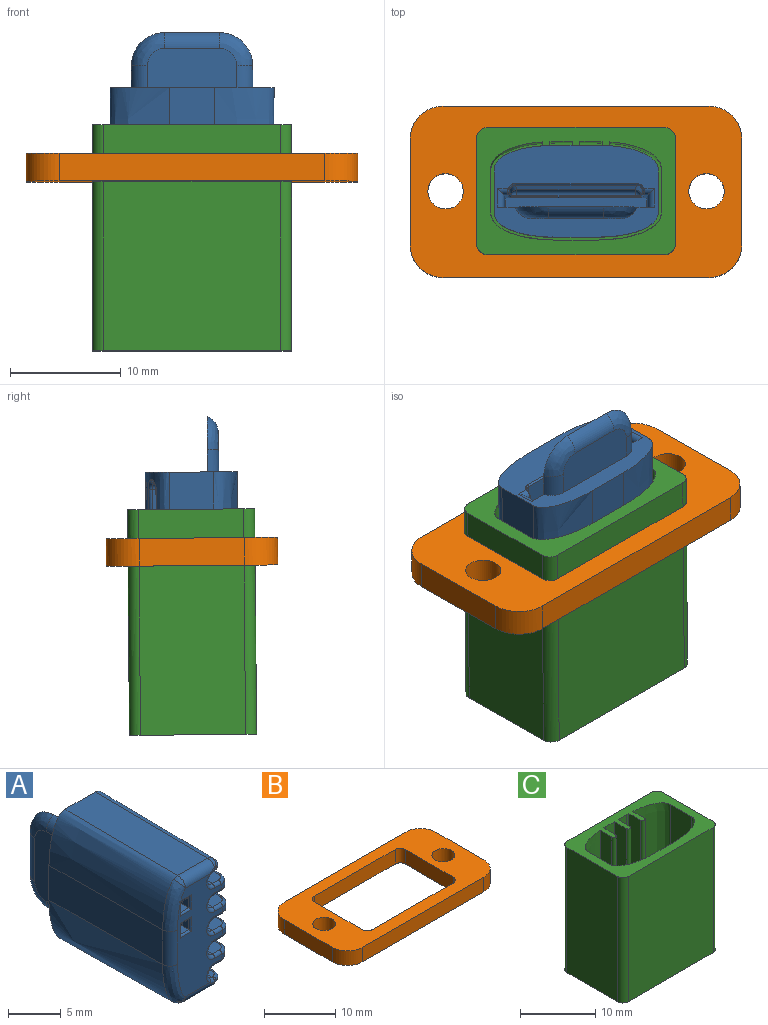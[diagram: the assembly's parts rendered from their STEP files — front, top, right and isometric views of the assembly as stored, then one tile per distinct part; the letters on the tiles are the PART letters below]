
ASSEMBLY  parts=3 mates=2
PART A: 179 faces, bbox 8.4x21.2x14.9 mm
  f0: bspline ~0.31x0.21mm, area 0.1mm2, adj f19,f94,f103,f104
  f1: bspline ~1.11x1mm, area 0.9mm2, adj f13,f20,f159,f178
  f2: cylinder r=1mm len=1mm, axis (0,0,1), area 0.9mm2, adj f18,f20,f138,f155
  f3: bspline ~0.91x0.75mm, area 0.3mm2, adj f17,f51,f134
  f4: plane 8.34x1.18mm, normal (0,-0.02,1), area 5.8mm2, adj f9,f21,f29,f37,f40,f53,f54
  f5: plane 8.34x1.18mm, normal (0,-0.02,-1), area 5.8mm2, adj f9,f21,f29,f37,f40,f53,f56
  f6: plane 8.34x1.18mm, normal (0,-0.02,1), area 5.8mm2, adj f8,f21,f28,f38,f39,f60,f62
  f7: plane 8.34x1.18mm, normal (0,-0.02,-1), area 5.8mm2, adj f8,f21,f28,f38,f39,f59,f60
  f8: plane 1x0.02mm, normal (0.01,-1,0), area 0mm2, adj f6,f7,f21,f39
  f9: plane 1x0.02mm, normal (0.01,-1,0), area 0mm2, adj f4,f5,f21,f40
  f10: plane 12.79x0.85mm, normal (0,1,0), area 10.9mm2, adj f21,f22,f23,f26,f28,f29
  f11: bspline ~16.06x5.41mm, area 92.3mm2, adj f14,f15,f19,f42,f44
  f12: bspline ~16.06x5.41mm, area 92.3mm2, adj f15,f16,f19,f48,f50
  f13: bspline ~16.06x5.41mm, area 34.3mm2, adj f1,f14,f18,f19,f43,f45,f156,f157
  f14: plane 15.07x4.02mm, normal (0,-0.01,-1), area 60.5mm2, adj f11,f13,f19,f41
  f15: plane 15.07x4.02mm, normal (-1,-0.01,0), area 60.5mm2, adj f11,f12,f19,f46
  f16: plane 15.07x4.02mm, normal (0,-0.01,1), area 60.5mm2, adj f12,f17,f19,f52
  f17: bspline ~16.06x5.41mm, area 34.3mm2, adj f3,f16,f18,f19,f49,f51,f124,f126
  f18: plane 15.1x4.04mm, normal (1,-0.01,0), area 23.2mm2, adj f2,f13,f17,f19,f47,f135,f136,f146
  f19: plane 14.85x8.32mm, normal (0,1,0), area 73.6mm2, adj f0,f11,f12,f13,f14,f15,f16,f17
  f20: plane 12.57x6.04mm, normal (0,-1,0), area 47.9mm2, adj f1,f2,f41,f44,f46,f47,f48,f49
  f21: plane 20.08x14.17mm, normal (1,0.01,0), area 228.8mm2, adj f4,f5,f6,f7,f8,f9,f10,f19
  f22: plane 14.51x1.11mm, normal (0,0.01,-1), area 14.2mm2, adj f10,f21,f23,f69
  f23: plane 14.54x13.07mm, normal (-1,0.01,0), area 14.7mm2, adj f10,f22,f26,f32,f33,f34,f35,f36
  f24: plane 13.79x0.28mm, normal (0,0.01,-1), area 1.4mm2, adj f31,f32,f98,f100
  f25: plane 13.79x0.28mm, normal (0,0.01,1), area 1.4mm2, adj f30,f36,f94,f106
  f26: plane 14.51x1.11mm, normal (0,0.01,1), area 14.2mm2, adj f10,f21,f23,f71
  f27: plane 10.7x0.05mm, normal (0,1,0), area 0.5mm2, adj f30,f31,f34,f96
  f28: plane 1.3x0.81mm, normal (-1,-0.01,0), area 1mm2, adj f6,f7,f10,f60
  f29: plane 1.3x0.81mm, normal (-1,-0.01,0), area 1mm2, adj f4,f5,f10,f53
  f30: cylinder r=0.55mm len=0.55mm, axis (1,0,0), area 0mm2, adj f25,f27,f35,f95
  f31: cylinder r=0.55mm len=0.55mm, axis (-1,0,0), area 0mm2, adj f24,f27,f33,f97
  f32: cylinder r=0.15mm len=13.49mm, axis (-0.01,-1,-0.01), area 3.2mm2, adj f23,f24,f33,f99
  f33: bspline ~0.7x0.7mm, area 0.2mm2, adj f23,f31,f32,f34
  f34: cylinder r=0.15mm len=10.7mm, axis (0,0,-1), area 2.5mm2, adj f23,f27,f33,f35
  f35: bspline ~0.7x0.7mm, area 0.2mm2, adj f23,f30,f34,f36
  f36: cylinder r=0.15mm len=13.49mm, axis (-0.01,-1,0.01), area 3.2mm2, adj f23,f25,f35,f107
  f37: plane 8.17x1.3mm, normal (0.99,-0.11,0), area 9.5mm2, adj f4,f5,f40,f54,f56,f57,f58
  f38: plane 8.17x1.3mm, normal (0.99,-0.11,0), area 9.5mm2, adj f6,f7,f39,f59,f61,f62
  f39: cylinder r=0.2mm len=1.01mm, axis (0,0,1), area 0.3mm2, adj f6,f7,f8,f38
  f40: cylinder r=0.2mm len=1.01mm, axis (0,0,-1), area 0.3mm2, adj f4,f5,f9,f37
  f41: cylinder r=1mm len=4.02mm, axis (1,0,0), area 6.1mm2, adj f14,f20,f42,f43,f171,f173
  f42: bspline ~1x1mm, area 0.6mm2, adj f11,f41,f44
  f43: bspline ~0.94x0.73mm, area 0.5mm2, adj f13,f41,f45,f169
  f44: bspline ~5.13x2.08mm, area 8mm2, adj f11,f20,f42,f46
  f45: bspline ~0.91x0.76mm, area 0.3mm2, adj f13,f43,f167
  f46: cylinder r=1mm len=4.02mm, axis (0,0,-1), area 6.3mm2, adj f15,f20,f44,f48
  f47: cylinder r=1mm len=1mm, axis (0,0,1), area 0.9mm2, adj f18,f20,f148,f166
  f48: bspline ~5.09x2.07mm, area 8mm2, adj f12,f20,f46,f50,f55,f58
  f49: bspline ~1.11x1mm, area 0.9mm2, adj f17,f20,f123,f145
  f50: bspline ~1x1mm, area 0.4mm2, adj f12,f48,f52
  f51: bspline ~0.94x0.73mm, area 0.5mm2, adj f3,f17,f52,f133
  f52: cylinder r=1mm len=4.02mm, axis (-1,0,0), area 6.1mm2, adj f16,f20,f50,f51,f129,f131
  f53: cylinder r=0.2mm len=1.7mm, axis (0,0,1), area 0.5mm2, adj f4,f5,f20,f29,f54,f56
  f54: cylinder r=0.2mm len=1.58mm, axis (1,0,0), area 0.4mm2, adj f4,f20,f37,f53,f57
  f55: bspline ~0.11x0.1mm, area 0mm2, adj f48,f56,f58
  f56: cylinder r=0.2mm len=1.5mm, axis (-1,0,0), area 0.4mm2, adj f5,f20,f37,f53,f55,f58
  f57: cylinder r=0.2mm len=1.4mm, axis (0,0,-1), area 0.4mm2, adj f20,f37,f54,f58
  f58: bspline ~0.3x0.22mm, area 0.1mm2, adj f37,f48,f55,f56,f57
  f59: cylinder r=0.2mm len=1.58mm, axis (-1,0,0), area 0.4mm2, adj f7,f20,f38,f60,f61
  f60: cylinder r=0.2mm len=1.7mm, axis (0,0,1), area 0.5mm2, adj f6,f7,f20,f28,f59,f62
  f61: cylinder r=0.2mm len=1.7mm, axis (0,0,-1), area 0.4mm2, adj f20,f38,f59,f62
  f62: cylinder r=0.2mm len=1.58mm, axis (1,0,0), area 0.4mm2, adj f6,f20,f38,f60,f61
  f63: plane 8.07x3.57mm, normal (-1,0.01,0), area 27.7mm2, adj f19,f64,f65,f66,f67,f68
  f64: cylinder r=1.56mm len=2.05mm, axis (0.01,1,0), area 3.9mm2, adj f19,f21,f63,f65
  f65: bspline ~3x2.97mm, area 6.9mm2, adj f21,f63,f64,f66
  f66: cylinder r=1.56mm len=4.98mm, axis (0,0,-1), area 9.2mm2, adj f21,f63,f65,f67
  f67: bspline ~3x2.97mm, area 6.9mm2, adj f21,f63,f66,f68
  f68: cylinder r=1.56mm len=2.04mm, axis (0.01,1,0), area 3.9mm2, adj f19,f21,f63,f67
  f69: cylinder r=0.55mm len=1.66mm, axis (1,0,0), area 1.2mm2, adj f19,f21,f22,f70
  f70: cylinder r=0.55mm len=0.94mm, axis (0,0,-1), area 0.5mm2, adj f19,f23,f69,f99,f100,f101
  f71: cylinder r=0.55mm len=1.66mm, axis (-1,0,0), area 1.2mm2, adj f19,f21,f26,f72
  f72: cylinder r=0.55mm len=0.94mm, axis (0,0,-1), area 0.5mm2, adj f19,f23,f71,f105,f106,f107
  f73: plane 13.87x10.94mm, normal (-1,0.02,0), area 150.1mm2, adj f94,f96,f98,f103
  f74: plane 1.89x0.11mm, normal (0,-1,0), area 0.2mm2, adj f117,f118,f119,f139
  f75: cone r=0.6mm half-angle=0.5deg, axis (0,-1,0), area 29.7mm2, adj f76,f77,f118,f142
  f76: plane 14.17x1.85mm, normal (0,-0.01,1), area 25.2mm2, adj f75,f119,f136,f138,f140
  f77: plane 14.17x1.74mm, normal (0,-0.01,-1), area 23.6mm2, adj f75,f117,f143,f144,f145
  f78: plane 1.43x0.11mm, normal (0,-1,0), area 0.1mm2, adj f120,f121,f122,f128
  f79: cone r=0.6mm half-angle=0.5deg, axis (0,-1,0), area 29.7mm2, adj f80,f81,f121,f127,f129
  f80: plane 14.18x0.97mm, normal (0,-0.01,-1), area 11.3mm2, adj f79,f120,f131,f132,f133,f134
  f81: plane 14.18x1.61mm, normal (0,-0.01,1), area 22mm2, adj f79,f122,f123,f124,f125
  f82: plane 1.89x0.11mm, normal (0,-1,0), area 0.2mm2, adj f111,f112,f113,f158
  f83: cone r=0.6mm half-angle=0.5deg, axis (0,-1,0), area 29.7mm2, adj f84,f85,f112,f163
  f84: plane 14.17x1.74mm, normal (0,-0.01,1), area 23.6mm2, adj f83,f113,f157,f159,f161
  f85: plane 14.17x1.85mm, normal (0,-0.01,-1), area 25.2mm2, adj f83,f111,f164,f165,f166
  f86: plane 1.91x0.11mm, normal (0,-1,0), area 0.2mm2, adj f114,f115,f116,f149
  f87: cone r=0.6mm half-angle=0.5deg, axis (0,-1,0), area 29.7mm2, adj f88,f89,f115,f152
  f88: plane 14.17x1.85mm, normal (0,-0.01,-1), area 25.2mm2, adj f87,f114,f153,f154,f155
  f89: plane 14.17x1.85mm, normal (0,-0.01,1), area 25.2mm2, adj f87,f116,f146,f148,f150
  f90: plane 1.43x0.11mm, normal (0,-1,0), area 0.1mm2, adj f108,f109,f110,f172
  f91: cone r=0.6mm half-angle=0.5deg, axis (0,-1,0), area 29.7mm2, adj f92,f93,f109,f173,f175
  f92: plane 14.18x1.61mm, normal (0,-0.01,-1), area 22mm2, adj f91,f108,f176,f177,f178
  f93: plane 14.18x0.97mm, normal (0,-0.01,1), area 11.3mm2, adj f91,f110,f167,f168,f169,f171
  f94: cylinder r=0.55mm len=13.88mm, axis (0.02,1,-0.01), area 12mm2, adj f0,f25,f73,f95,f104,f105
  f95: sphere r=0.55mm, area 0.3mm2, adj f30,f94,f96
  f96: cylinder r=0.55mm len=10.7mm, axis (0,0,1), area 9.2mm2, adj f27,f73,f95,f97
  f97: sphere r=0.55mm, area 0.3mm2, adj f31,f96,f98
  f98: cylinder r=0.55mm len=13.87mm, axis (-0.02,-1,-0.01), area 12mm2, adj f24,f73,f97,f101,f102
  f99: cylinder r=0.15mm len=0.15mm, axis (0.01,1,0.01), area 0mm2, adj f32,f70,f100
  f100: bspline ~0.42x0.32mm, area 0.1mm2, adj f24,f70,f99,f101
  f101: bspline ~0.32x0.22mm, area 0.1mm2, adj f70,f98,f100,f102
  f102: bspline ~0.66x0.52mm, area 0.2mm2, adj f19,f98,f101,f103
  f103: cylinder r=0.15mm len=10.94mm, axis (0,0,1), area 2.5mm2, adj f0,f19,f73,f102
  f104: bspline ~0.44x0.42mm, area 0.1mm2, adj f0,f19,f94,f105
  f105: bspline ~0.32x0.22mm, area 0.1mm2, adj f72,f94,f104,f106
  f106: bspline ~0.42x0.32mm, area 0.1mm2, adj f25,f72,f105,f107
  f107: bspline ~0.15x0.15mm, area 0mm2, adj f36,f72,f106
  f108: cylinder r=0.55mm len=1.61mm, axis (-1,0,0), area 1.3mm2, adj f90,f92,f109,f174
  f109: torus R=0.05mm, axis (0,1,0), area 1.1mm2, adj f90,f91,f108,f110
  f110: cylinder r=0.55mm len=1.34mm, axis (1,0,0), area 1mm2, adj f90,f93,f109,f170
  f111: cylinder r=0.55mm len=1.85mm, axis (-1,0,0), area 1.6mm2, adj f82,f85,f112,f160,f162
  f112: torus R=0.05mm, axis (0,1,0), area 1.1mm2, adj f82,f83,f111,f113
  f113: cylinder r=0.55mm len=1.83mm, axis (1,0,0), area 1.5mm2, adj f82,f84,f112,f156
  f114: cylinder r=0.55mm len=1.85mm, axis (-1,0,0), area 1.6mm2, adj f86,f88,f115,f151
  f115: torus R=0.05mm, axis (0,1,0), area 1.1mm2, adj f86,f87,f114,f116
  f116: cylinder r=0.55mm len=1.85mm, axis (1,0,0), area 1.6mm2, adj f86,f89,f115,f147
  f117: cylinder r=0.55mm len=1.83mm, axis (-1,0,0), area 1.5mm2, adj f74,f77,f118,f141
  f118: torus R=0.05mm, axis (0,1,0), area 1.1mm2, adj f74,f75,f117,f119
  f119: cylinder r=0.55mm len=1.85mm, axis (1,0,0), area 1.6mm2, adj f74,f76,f118,f135,f137
  f120: cylinder r=0.55mm len=1.34mm, axis (-1,0,0), area 1mm2, adj f78,f80,f121,f130
  f121: torus R=0.05mm, axis (0,1,0), area 1.1mm2, adj f78,f79,f120,f122
  f122: cylinder r=0.55mm len=1.61mm, axis (1,0,0), area 1.3mm2, adj f78,f81,f121,f126
  f123: bspline ~1.01x1mm, area 0.7mm2, adj f49,f81,f124,f125
  f124: cylinder r=0.35mm len=13.52mm, axis (0.01,1,0.01), area 6.5mm2, adj f17,f81,f123,f126
  f125: cylinder r=0.35mm len=0.84mm, axis (-1,0,0), area 0.5mm2, adj f20,f81,f123,f127
  f126: bspline ~0.94x0.9mm, area 0.6mm2, adj f17,f122,f124,f128
  f127: torus R=1.08mm, axis (0,1,0), area 1.2mm2, adj f20,f79,f125,f129
  f128: cylinder r=0.35mm len=0.37mm, axis (-0.32,0,0.95), area 0.1mm2, adj f17,f78,f126,f130
  f129: bspline ~0.65x0.62mm, area 0.4mm2, adj f52,f79,f127,f131
  f130: bspline ~1.09x0.9mm, area 0.7mm2, adj f17,f120,f128,f132
  f131: cylinder r=0.35mm len=0.47mm, axis (-1,0,0), area 0mm2, adj f52,f80,f129,f133
  f132: bspline ~13.53x0.85mm, area 10.2mm2, adj f17,f80,f130,f134
  f133: bspline ~0.51x0.47mm, area 0.1mm2, adj f51,f80,f131,f134
  f134: bspline ~0.93x0.88mm, area 0.9mm2, adj f3,f80,f132,f133
  f135: bspline ~0.62x0.5mm, area 0.3mm2, adj f18,f119,f136,f137
  f136: cylinder r=0.35mm len=13.52mm, axis (0.01,1,0.01), area 7.4mm2, adj f18,f76,f135,f138
  f137: bspline ~0.67x0.52mm, area 0.3mm2, adj f17,f119,f135,f139
  f138: bspline ~1x1mm, area 0.7mm2, adj f2,f76,f136,f140
  f139: cylinder r=0.35mm len=0.36mm, axis (-0.05,0,1), area 0.1mm2, adj f17,f74,f137,f141
  f140: cylinder r=0.35mm len=1.07mm, axis (-1,0,0), area 0.6mm2, adj f20,f76,f138,f142
  f141: bspline ~0.95x0.9mm, area 0.6mm2, adj f17,f117,f139,f143
  f142: torus R=1.08mm, axis (0,1,0), area 1.5mm2, adj f20,f75,f140,f144
  f143: cylinder r=0.35mm len=13.52mm, axis (-0.01,-1,0.01), area 8.1mm2, adj f17,f77,f141,f145
  f144: cylinder r=0.35mm len=0.94mm, axis (1,0,0), area 0.5mm2, adj f20,f77,f142,f145
  f145: bspline ~1.01x1mm, area 0.8mm2, adj f49,f77,f143,f144
  f146: cylinder r=0.35mm len=13.52mm, axis (0.01,1,0.01), area 7.4mm2, adj f18,f89,f147,f148
  f147: bspline ~0.9x0.9mm, area 0.6mm2, adj f18,f116,f146,f149
  f148: bspline ~1x1mm, area 0.7mm2, adj f47,f89,f146,f150
  f149: cylinder r=0.35mm len=0.35mm, axis (0,0,1), area 0.1mm2, adj f18,f86,f147,f151
  f150: cylinder r=0.35mm len=1.07mm, axis (-1,0,0), area 0.6mm2, adj f20,f89,f148,f152
  f151: bspline ~0.9x0.9mm, area 0.6mm2, adj f18,f114,f149,f153
  f152: torus R=1.08mm, axis (0,1,0), area 1.5mm2, adj f20,f87,f150,f154
  f153: cylinder r=0.35mm len=13.52mm, axis (-0.01,-1,0.01), area 7.4mm2, adj f18,f88,f151,f155
  f154: cylinder r=0.35mm len=1.07mm, axis (1,0,0), area 0.6mm2, adj f20,f88,f152,f155
  f155: bspline ~1x1mm, area 0.7mm2, adj f2,f88,f153,f154
  f156: bspline ~0.95x0.9mm, area 0.6mm2, adj f13,f113,f157,f158
  f157: cylinder r=0.35mm len=13.52mm, axis (0.01,1,0.01), area 8.1mm2, adj f13,f84,f156,f159
  f158: cylinder r=0.35mm len=0.36mm, axis (0.05,0,1), area 0.1mm2, adj f13,f82,f156,f160
  f159: bspline ~1.06x1mm, area 0.8mm2, adj f1,f84,f157,f161
  f160: bspline ~0.67x0.52mm, area 0.3mm2, adj f13,f111,f158,f162
  f161: cylinder r=0.35mm len=0.94mm, axis (-1,0,0), area 0.5mm2, adj f20,f84,f159,f163
  f162: bspline ~0.62x0.5mm, area 0.3mm2, adj f18,f111,f160,f164
  f163: torus R=1.08mm, axis (0,1,0), area 1.5mm2, adj f20,f83,f161,f165
  f164: cylinder r=0.35mm len=13.52mm, axis (-0.01,-1,0.01), area 7.4mm2, adj f18,f85,f162,f166
  f165: cylinder r=0.35mm len=1.07mm, axis (1,0,0), area 0.6mm2, adj f20,f85,f163,f166
  f166: bspline ~1x1mm, area 0.7mm2, adj f47,f85,f164,f165
  f167: bspline ~1.23x1.07mm, area 0.9mm2, adj f45,f93,f168,f169
  f168: bspline ~13.53x0.85mm, area 10.2mm2, adj f13,f93,f167,f170
  f169: bspline ~0.47x0.37mm, area 0.1mm2, adj f43,f93,f167,f171
  f170: bspline ~1.09x0.9mm, area 0.7mm2, adj f13,f110,f168,f172
  f171: cylinder r=0.35mm len=0.47mm, axis (1,0,0), area 0mm2, adj f41,f93,f169,f173
  f172: cylinder r=0.35mm len=0.37mm, axis (0.32,0,0.95), area 0.1mm2, adj f13,f90,f170,f174
  f173: bspline ~0.65x0.62mm, area 0.4mm2, adj f41,f91,f171,f175
  f174: bspline ~0.94x0.9mm, area 0.6mm2, adj f13,f108,f172,f176
  f175: torus R=1.08mm, axis (0,1,0), area 1.2mm2, adj f20,f91,f173,f177
  f176: cylinder r=0.35mm len=13.52mm, axis (-0.01,-1,0.01), area 6.5mm2, adj f13,f92,f174,f178
  f177: cylinder r=0.35mm len=0.84mm, axis (1,0,0), area 0.5mm2, adj f20,f92,f175,f178
  f178: bspline ~1.01x1mm, area 0.7mm2, adj f1,f92,f176,f177
PART B: 20 faces, bbox 30x15.5x2.5 mm
  f0: plane 24x2.5mm, normal (0,-1,0), area 60mm2, adj f1,f17,f18,f19
  f1: cylinder r=3mm len=3mm, axis (0,0,1), area 11.8mm2, adj f0,f2,f18,f19
  f2: plane 9.5x2.5mm, normal (1,0,0), area 23.8mm2, adj f1,f3,f18,f19
  f3: cylinder r=3mm len=3mm, axis (0,0,1), area 11.8mm2, adj f2,f4,f18,f19
  f4: plane 24x2.5mm, normal (0,1,0), area 60mm2, adj f3,f5,f18,f19
  f5: cylinder r=3mm len=3mm, axis (0,0,1), area 11.8mm2, adj f4,f6,f18,f19
  f6: plane 9.5x2.5mm, normal (-1,0,0), area 23.8mm2, adj f5,f17,f18,f19
  f7: cylinder r=1mm len=2.5mm, axis (0,0,1), area 3.9mm2, adj f8,f14,f18,f19
  f8: plane 9.5x2.5mm, normal (-1,0,0), area 23.8mm2, adj f7,f9,f18,f19
  f9: cylinder r=1mm len=2.5mm, axis (0,0,1), area 3.9mm2, adj f8,f10,f18,f19
  f10: plane 16x2.5mm, normal (0,1,0), area 40mm2, adj f9,f11,f18,f19
  f11: cylinder r=1mm len=2.5mm, axis (0,0,1), area 3.9mm2, adj f10,f12,f18,f19
  f12: plane 9.5x2.5mm, normal (1,0,0), area 23.8mm2, adj f11,f13,f18,f19
  f13: cylinder r=1mm len=2.5mm, axis (0,0,1), area 3.9mm2, adj f12,f14,f18,f19
  f14: plane 16x2.5mm, normal (0,-1,0), area 40mm2, adj f7,f13,f18,f19
  f15: cylinder r=1.6mm len=3.2mm, axis (0,0,1), area 25.1mm2, adj f18,f19
  f16: cylinder r=1.6mm len=3.2mm, axis (0,0,1), area 25.1mm2, adj f18,f19
  f17: cylinder r=3mm len=3mm, axis (0,0,1), area 11.8mm2, adj f0,f6,f18,f19
  f18: plane 30x15.5mm, normal (0,0,-1), area 235mm2, adj f0,f1,f2,f3,f4,f5,f6,f7
  f19: plane 30x15.5mm, normal (0,0,1), area 235mm2, adj f0,f1,f2,f3,f4,f5,f6,f7
PART C: 53 faces, bbox 18x11.5x20.4 mm
  f0: plane 5.6x2.6mm, normal (0,-1,0), area 14.6mm2, adj f1,f3,f43,f44
  f1: plane 3.15x2.6mm, normal (1,0,0), area 8.2mm2, adj f0,f2,f43,f44
  f2: plane 5.6x2.6mm, normal (0,1,0), area 14.6mm2, adj f1,f3,f43,f44
  f3: plane 3.15x2.6mm, normal (-1,0,0), area 8.2mm2, adj f0,f2,f43,f44
  f4: plane 18x11.5mm, normal (0,0,-1), area 56.1mm2, adj f17,f18,f19,f20,f21,f22,f23,f24
  f5: extruded ~13.2x0.35mm, area 4.6mm2, adj f7,f25,f27,f40
  f6: extruded ~13.2x4.66mm, area 74.5mm2, adj f7,f25,f33,f37
  f7: plane 15.44x8.92mm, normal (0,0,1), area 117.5mm2, adj f5,f6,f8,f9,f10,f11,f12,f13
  f8: plane 13.2x1.66mm, normal (0,-1,0), area 21.9mm2, adj f7,f25,f26,f35
  f9: plane 2.6x1.4mm, normal (0,-1,0), area 3.6mm2, adj f7,f10,f15,f43
  f10: plane 2.6x1.18mm, normal (-1,0,0), area 3.1mm2, adj f7,f9,f11,f43
  f11: plane 2.6x1.4mm, normal (0,1,0), area 3.6mm2, adj f7,f10,f15,f43
  f12: plane 2.6x1.4mm, normal (0,-1,0), area 3.6mm2, adj f7,f13,f16,f43
  f13: plane 2.6x1.18mm, normal (-1,0,0), area 3.1mm2, adj f7,f12,f14,f43
  f14: plane 2.6x1.4mm, normal (0,1,0), area 3.6mm2, adj f7,f13,f16,f43
  f15: plane 2.6x1.18mm, normal (1,0,0), area 3.1mm2, adj f7,f9,f11,f43
  f16: plane 2.6x1.18mm, normal (1,0,0), area 3.1mm2, adj f7,f12,f14,f43
  f17: plane 20.4x16mm, normal (0,-1,0), area 326.4mm2, adj f4,f18,f24,f25
  f18: cylinder r=1mm len=20.4mm, axis (0,0,1), area 32mm2, adj f4,f17,f19,f25
  f19: plane 20.4x9.5mm, normal (1,0,0), area 193.8mm2, adj f4,f18,f20,f25
  f20: cylinder r=1mm len=20.4mm, axis (0,0,1), area 32mm2, adj f4,f19,f21,f25
  f21: plane 20.4x16mm, normal (0,1,0), area 326.4mm2, adj f4,f20,f22,f25
  f22: cylinder r=1mm len=20.4mm, axis (0,0,1), area 32mm2, adj f4,f21,f23,f25
  f23: plane 20.4x9.5mm, normal (-1,0,0), area 193.8mm2, adj f4,f22,f24,f25
  f24: cylinder r=1mm len=20.4mm, axis (0,0,1), area 32mm2, adj f4,f17,f23,f25
  f25: plane 18x11.5mm, normal (0,0,1), area 85.3mm2, adj f5,f6,f8,f17,f18,f19,f20,f21
  f26: extruded ~13.2x0.35mm, area 4.6mm2, adj f7,f8,f25,f38
  f27: plane 13.2x1.66mm, normal (0,-1,0), area 21.9mm2, adj f5,f7,f25,f36
  f28: extruded ~13.2x4.66mm, area 74.5mm2, adj f7,f25,f29,f41
  f29: plane 13.2x4.01mm, normal (1,0,0), area 53mm2, adj f7,f25,f28,f30
  f30: extruded ~13.2x5.71mm, area 88.4mm2, adj f7,f25,f29,f31
  f31: plane 13.2x4.02mm, normal (0,1,0), area 53.1mm2, adj f7,f25,f30,f32
  f32: extruded ~13.2x5.71mm, area 88.4mm2, adj f7,f25,f31,f33
  f33: plane 13.2x4.01mm, normal (-1,0,0), area 53mm2, adj f6,f7,f25,f32
  f34: cylinder r=0.35mm len=13.2mm, axis (0,0,1), area 14.5mm2, adj f7,f25,f35,f36
  f35: plane 13.2x2.25mm, normal (1,0,0), area 29.6mm2, adj f7,f8,f25,f34
  f36: plane 13.2x2.25mm, normal (-1,0,0), area 29.6mm2, adj f7,f25,f27,f34
  f37: plane 13.2x2.2mm, normal (1,0,0), area 29.1mm2, adj f6,f7,f25,f39
  f38: plane 13.2x2.24mm, normal (-1,0,0), area 29.5mm2, adj f7,f25,f26,f39
  f39: cylinder r=0.35mm len=13.2mm, axis (0,0,1), area 14.5mm2, adj f7,f25,f37,f38
  f40: plane 13.2x2.24mm, normal (1,0,0), area 29.5mm2, adj f5,f7,f25,f42
  f41: plane 13.2x2.2mm, normal (-1,0,0), area 29.1mm2, adj f7,f25,f28,f42
  f42: cylinder r=0.35mm len=13.2mm, axis (0,0,1), area 14.5mm2, adj f7,f25,f40,f41
  f43: plane 5.6x3.15mm, normal (0,0,-1), area 14.3mm2, adj f0,f1,f2,f3,f9,f10,f11,f12
  f44: plane 16x9.5mm, normal (0,0,-1), area 132.4mm2, adj f0,f1,f2,f3,f45,f46,f47,f48
  f45: plane 6.5x2mm, normal (-1,0,0), area 13mm2, adj f4,f44,f46,f52
  f46: cylinder r=1.5mm len=2mm, axis (0,0,-1), area 4.7mm2, adj f4,f44,f45,f47
  f47: plane 13x2mm, normal (0,1,0), area 26mm2, adj f4,f44,f46,f48
  f48: cylinder r=1.5mm len=2mm, axis (0,0,-1), area 4.7mm2, adj f4,f44,f47,f49
  f49: plane 6.5x2mm, normal (1,0,0), area 13mm2, adj f4,f44,f48,f50
  f50: cylinder r=1.5mm len=2mm, axis (0,0,-1), area 4.7mm2, adj f4,f44,f49,f51
  f51: plane 13x2mm, normal (0,-1,0), area 26mm2, adj f4,f44,f50,f52
  f52: cylinder r=1.5mm len=2mm, axis (0,0,-1), area 4.7mm2, adj f4,f44,f45,f51
PLACE A rot(axis=(0.58,0.58,0.58),119.7deg) t=(-20.75,-15.07,26.8)mm
PLACE B rot(axis=(-1,0,0),0.5deg) t=(-9.26,-15.7,36.88)mm
PLACE C rot(axis=(-1,0,0),0.5deg) t=(-9.26,-15.7,36.88)mm
MATE slider A.f20 <-> C.f7  axis (0,-0.01,-1) through (-21.09,-15.58,26.77)mm
MATE fastened B.f10 <-> C.f17  axis (0,1,-0.01) through (-20.76,-20.68,36.92)mm
